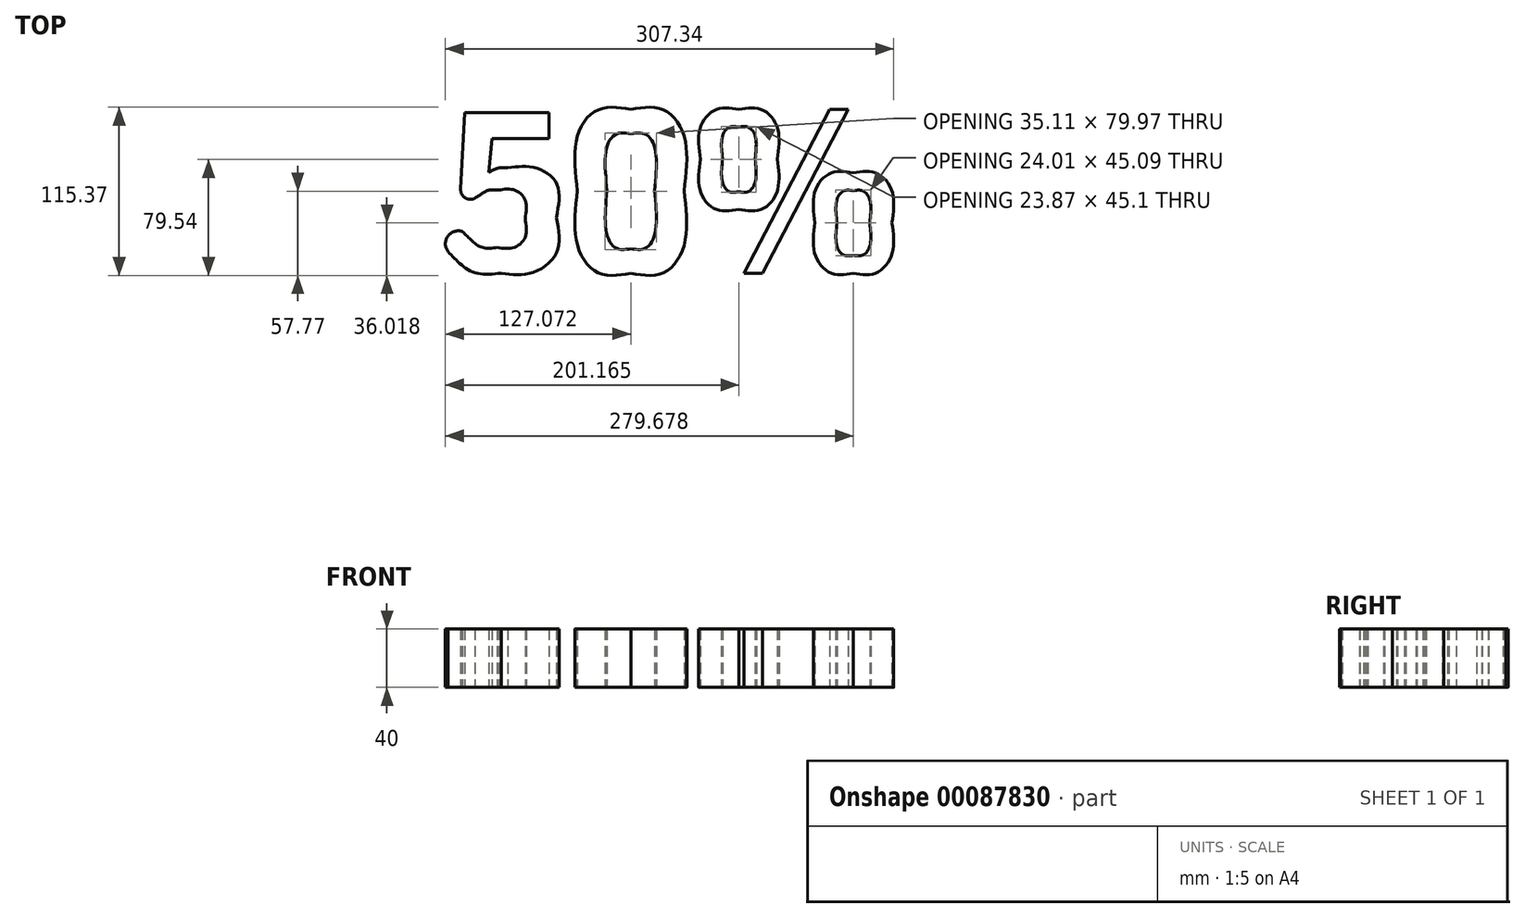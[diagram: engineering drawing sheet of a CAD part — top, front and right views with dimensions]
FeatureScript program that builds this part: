
annotation { "Feature Type Name" : "Feature", "Feature Type Description" : "" }
export const myFeature = defineFeature(function(context is Context, id is Id, definition is map)
    precondition{}
    {
        {
            var Q0;
            Q0=qCreatedBy(makeId("Front.planeOp"),FACE);
            var sketch = newSketch(context, id + "F0", { "sketchPlane" : qUnion([Q0])});
            skText(sketch, "E0", { "text": "50%", "fontName": "NotoSansCJKjp-Bold.otf"});
            const initialGuessF0  = {"E0": [-0.11078, -0.05871, 1, 0, 0.10519]};
            skSetInitialGuess(sketch, initialGuessF0);
            skSolve(sketch);
        }
        {
            var Q0;
            Q0=qCreatedBy(makeId("Top.planeOp"),FACE);
            var sketch = newSketch(context, id + "F1", { "sketchPlane" : qUnion([Q0])});
            skLineSegment(sketch, "E1.0", {"start": v(-95.44, 49.4) * mm, "end": v(-98.37, -3.06) * mm});
            skLineSegment(sketch, "E1.1", {"start": v(-37.6, 49.4) * mm, "end": v(-95.44, 49.4) * mm});
            skLineSegment(sketch, "E1.2", {"start": v(-37.6, 31.43) * mm, "end": v(-37.6, 49.4) * mm});
            skLineSegment(sketch, "E1.3", {"start": v(-76.89, 31.43) * mm, "end": v(-37.6, 31.43) * mm});
            skLineSegment(sketch, "E1.4", {"start": v(-78.94, 8.49) * mm, "end": v(-76.89, 31.43) * mm});
            skFitSpline(sketch, "E1.5", {"points": [v(-32.62, -22.79) * mm, v(-32.62, 0.75) * mm, v(-47.83, 11.55) * mm, v(-65.93, 11.55) * mm]});
            skFitSpline(sketch, "E1.6", {"points": [v(-65.93, 11.55) * mm, v(-70.9, 11.55) * mm, v(-74.7, 10.54) * mm, v(-78.94, 8.49) * mm]});
            skFitSpline(sketch, "E1.7", {"points": [v(-70.47, -60.77) * mm, v(-50.45, -60.77) * mm, v(-32.62, -46.9) * mm, v(-32.62, -22.79) * mm]});
            skFitSpline(sketch, "E1.8", {"points": [v(-107, -46) * mm, v(-98.96, -54.04) * mm, v(-87.55, -60.77) * mm, v(-70.47, -60.77) * mm]});
            skFitSpline(sketch, "E1.10", {"points": [v(-73.23, -43.24) * mm, v(-83.32, -43.24) * mm, v(-90.92, -38.26) * mm, v(-97.04, -32.28) * mm]});
            skFitSpline(sketch, "E1.11", {"points": [v(-54.1, -23.36) * mm, v(-54.1, -36.07) * mm, v(-61.98, -43.24) * mm, v(-73.23, -43.24) * mm]});
            skFitSpline(sketch, "E1.12", {"points": [v(-72.37, -3.8) * mm, v(-61.4, -3.8) * mm, v(-54.1, -10.8) * mm, v(-54.1, -23.36) * mm]});
            skFitSpline(sketch, "E1.13", {"points": [v(-88.57, -9.48) * mm, v(-82.3, -5.4) * mm, v(-78.78, -3.8) * mm, v(-72.37, -3.8) * mm]});
            skFitSpline(sketch, "E1.14", {"points": [v(18.37, 51.45) * mm, v(-3.68, 51.45) * mm, v(-18.29, 33.19) * mm, v(-18.29, -4.23) * mm]});
            skFitSpline(sketch, "E1.15", {"points": [v(54.9, -4.23) * mm, v(54.9, 33.03) * mm, v(40.28, 51.45) * mm, v(18.37, 51.45) * mm]});
            skFitSpline(sketch, "E1.16", {"points": [v(18.37, -60.77) * mm, v(40.28, -60.77) * mm, v(54.9, -41.48) * mm, v(54.9, -4.23) * mm]});
            skFitSpline(sketch, "E1.17", {"points": [v(-18.29, -4.23) * mm, v(-18.29, -41.48) * mm, v(-3.68, -60.77) * mm, v(18.37, -60.77) * mm]});
            skFitSpline(sketch, "E1.18", {"points": [v(18.37, -43.97) * mm, v(9.01, -43.97) * mm, v(2, -34.6) * mm, v(2, -4.23) * mm]});
            skFitSpline(sketch, "E1.19", {"points": [v(2, -4.23) * mm, v(2, 26.02) * mm, v(9.01, 34.78) * mm, v(18.37, 34.78) * mm]});
            skFitSpline(sketch, "E1.20", {"points": [v(18.37, 34.78) * mm, v(27.57, 34.78) * mm, v(34.58, 26.02) * mm, v(34.58, -4.23) * mm]});
            skFitSpline(sketch, "E1.21", {"points": [v(34.58, -4.23) * mm, v(34.58, -34.6) * mm, v(27.57, -43.97) * mm, v(18.37, -43.97) * mm]});
            skFitSpline(sketch, "E1.22", {"points": [v(92.3, 51.45) * mm, v(76.8, 51.45) * mm, v(66, 39.03) * mm, v(66, 17.39) * mm]});
            skFitSpline(sketch, "E1.23", {"points": [v(66, 17.39) * mm, v(66, -4.36) * mm, v(76.8, -17.08) * mm, v(92.3, -17.08) * mm]});
            skFitSpline(sketch, "E1.24", {"points": [v(92.3, -4.96) * mm, v(86.03, -4.96) * mm, v(81.19, 1.48) * mm, v(81.19, 17.39) * mm]});
            skFitSpline(sketch, "E1.25", {"points": [v(81.19, 17.39) * mm, v(81.19, 33.32) * mm, v(86.03, 39.3) * mm, v(92.3, 39.3) * mm]});
            skFitSpline(sketch, "E1.26", {"points": [v(92.3, 39.3) * mm, v(98.58, 39.3) * mm, v(103.56, 33.32) * mm, v(103.56, 17.39) * mm]});
            skFitSpline(sketch, "E1.27", {"points": [v(103.56, 17.39) * mm, v(103.56, 1.48) * mm, v(98.58, -4.96) * mm, v(92.3, -4.96) * mm]});
            skFitSpline(sketch, "E1.28", {"points": [v(118.74, 17.39) * mm, v(118.74, 39.03) * mm, v(107.78, 51.45) * mm, v(92.3, 51.45) * mm]});
            skFitSpline(sketch, "E1.29", {"points": [v(92.3, -17.08) * mm, v(107.78, -17.08) * mm, v(118.74, -4.36) * mm, v(118.74, 17.39) * mm]});
            skLineSegment(sketch, "E1.30", {"start": v(154.7, 51.45) * mm, "end": v(95.96, -60.77) * mm});
            skLineSegment(sketch, "E1.31", {"start": v(108.51, -60.77) * mm, "end": v(167.38, 51.45) * mm});
            skLineSegment(sketch, "E1.32", {"start": v(95.96, -60.77) * mm, "end": v(108.51, -60.77) * mm});
            skLineSegment(sketch, "E1.33", {"start": v(167.38, 51.45) * mm, "end": v(154.7, 51.45) * mm});
            skFitSpline(sketch, "E1.34", {"points": [v(197.33, -26.28) * mm, v(197.33, -4.52) * mm, v(186.24, 7.9) * mm, v(170.9, 7.9) * mm]});
            skFitSpline(sketch, "E1.35", {"points": [v(170.9, 7.9) * mm, v(155.56, 7.9) * mm, v(144.6, -4.52) * mm, v(144.6, -26.28) * mm]});
            skFitSpline(sketch, "E1.36", {"points": [v(144.6, -26.28) * mm, v(144.6, -47.9) * mm, v(155.56, -60.77) * mm, v(170.9, -60.77) * mm]});
            skFitSpline(sketch, "E1.37", {"points": [v(170.9, -60.77) * mm, v(186.24, -60.77) * mm, v(197.33, -47.9) * mm, v(197.33, -26.28) * mm]});
            skFitSpline(sketch, "E1.38", {"points": [v(182.15, -26.28) * mm, v(182.15, -42.21) * mm, v(177.18, -48.49) * mm, v(170.9, -48.49) * mm]});
            skFitSpline(sketch, "E1.39", {"points": [v(170.9, -4.23) * mm, v(177.18, -4.23) * mm, v(182.15, -10.37) * mm, v(182.15, -26.28) * mm]});
            skFitSpline(sketch, "E1.40", {"points": [v(159.64, -26.28) * mm, v(159.64, -10.37) * mm, v(164.62, -4.23) * mm, v(170.9, -4.23) * mm]});
            skFitSpline(sketch, "E1.41", {"points": [v(170.9, -48.49) * mm, v(164.62, -48.49) * mm, v(159.64, -42.21) * mm, v(159.64, -26.28) * mm]});
            skArc(sketch, "E2", {"start": v(-98.37, -3.06) * mm, "mid": v(-95.32, -9.1) * mm, "end": v(-88.57, -9.48) * mm});
            skArc(sketch, "E3", {"start": v(-97.04, -32.28) * mm, "mid": v(-107.1, -35.46) * mm, "end": v(-107, -46) * mm});
            skSolve(sketch);
        }
        {
            var Q0;
            Q0 = qSketchRegion(id + "F1", true);
            extrude(context, id + "F2", {"entities" : qUnion([Q0]), "depth" : 40 * mm});
        }
    });
